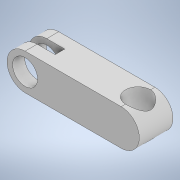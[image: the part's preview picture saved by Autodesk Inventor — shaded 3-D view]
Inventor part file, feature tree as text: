
AUTODESK INVENTOR PART (.ipt)
format: ipt  version: 2022 (Build 260153000, 153)  size: 141,312 bytes
history: native  units: in
note: dims shown in document units (in); Inventor stores cm internally (conversion verified against a paired STEP export)
features: extrude x3, sketch x3
ambient origin geometry x8: Origin, YZ Plane, XZ Plane, XY Plane, X Axis, Y Axis, Z Axis, Center Point
bodies: Solid1 (feature_tree)
feature tree (6):
  extrude  "Extrusion1"  Depth=0.75in
  extrude  "Extrusion2"  Depth=2.0in
  extrude  "Extrusion3"  Depth=0.7in TaperAngle=0.0deg
  sketch  "Sketch1"  dims[d0=0.52in d1=0.75in]
  sketch  "Sketch2"  dims[d2=2.0in d3=2.0in]
  sketch  "Sketch3"  dims[d4=0.75in d6=0.7in d7=0.0in d8=0.1in d9=0.1in d10=0.75in d11=1.0125in d12=0.0in d13=0.52in d14=1.0125in d15=0.0in]
